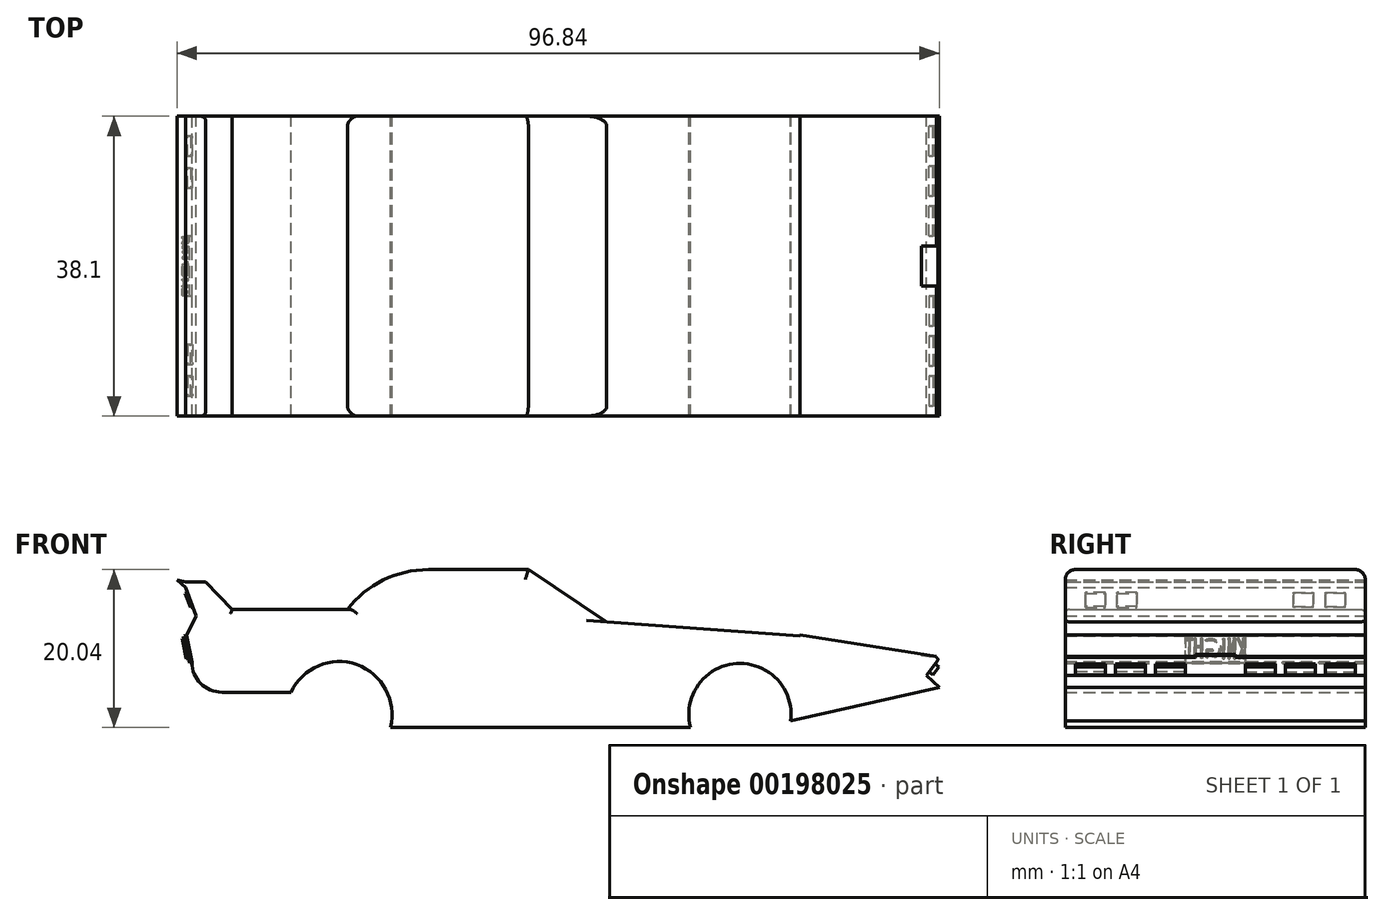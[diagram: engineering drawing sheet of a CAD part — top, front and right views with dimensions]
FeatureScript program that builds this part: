
annotation { "Feature Type Name" : "Feature", "Feature Type Description" : "" }
export const myFeature = defineFeature(function(context is Context, id is Id, definition is map)
    precondition{}
    {
        {
            var Q0;
            Q0=qCreatedBy(makeId("Front.planeOp"),FACE);
            var sketch = newSketch(context, id + "F0", { "sketchPlane" : qUnion([Q0])});
            skArc(sketch, "E0", {"start": v(4.17, 0.8) * mm, "mid": v(-2.68, 8.11) * mm, "end": v(-8.56, 0) * mm});
            skLineSegment(sketch, "E1", {"start": v(-8.56, 0) * mm, "end": v(-46.66, 0) * mm});
            skArc(sketch, "E2", {"start": v(-46.66, 0) * mm, "mid": v(-50.95, 7.97) * mm, "end": v(-59.3, 4.46) * mm});
            skLineSegment(sketch, "E3", {"start": v(-59.3, 4.46) * mm, "end": v(-68.07, 4.46) * mm});
            skLineSegment(sketch, "E4", {"start": v(-71.88, 8.27) * mm, "end": v(-72.57, 11.67) * mm});
            skLineSegment(sketch, "E5", {"start": v(-72.7, 18.5) * mm, "end": v(-70.16, 18.5) * mm});
            skLineSegment(sketch, "E6", {"start": v(-70.16, 18.5) * mm, "end": v(-66.76, 14.96) * mm});
            skLineSegment(sketch, "E7", {"start": v(-66.76, 14.96) * mm, "end": v(-52.11, 14.96) * mm});
            skLineSegment(sketch, "E8", {"start": v(-41.85, 20.04) * mm, "end": v(-29.15, 20.04) * mm});
            skArc(sketch, "E9", {"start": v(-41.85, 20.04) * mm, "mid": v(-47.58, 18.7) * mm, "end": v(-52.11, 14.96) * mm});
            skLineSegment(sketch, "E10", {"start": v(-29.15, 20.04) * mm, "end": v(-19.19, 13.37) * mm});
            skLineSegment(sketch, "E11", {"start": v(-19.19, 13.37) * mm, "end": v(5.34, 11.62) * mm});
            skLineSegment(sketch, "E12", {"start": v(5.34, 11.62) * mm, "end": v(23.06, 8.8) * mm});
            skLineSegment(sketch, "E13", {"start": v(23.06, 5.06) * mm, "end": v(4.17, 0.8) * mm});
            skLineSegment(sketch, "E14", {"start": v(23.06, 8.8) * mm, "end": v(21.44, 6.62) * mm});
            skLineSegment(sketch, "E15", {"start": v(21.44, 6.62) * mm, "end": v(23.06, 5.06) * mm});
            skPoint(sketch, "E16.visualSharp", {"position": v(-71.88, 4.46) * mm});
            skArc(sketch, "E16.filletArc", {"start": v(-71.88, 8.27) * mm, "mid": v(-70.77, 5.57) * mm, "end": v(-68.07, 4.46) * mm});
            skPoint(sketch, "E17.orphan", {"position": v(-59.72, 0) * mm});
            skPoint(sketch, "E18.orphan", {"position": v(4.02, 0) * mm});
            skLineSegment(sketch, "E19", {"start": v(-72.7, 18.5) * mm, "end": v(-73.78, 18.73) * mm});
            skLineSegment(sketch, "E20", {"start": v(-73.78, 18.73) * mm, "end": v(-72.7, 17.78) * mm});
            skLineSegment(sketch, "E21", {"start": v(-72.57, 11.67) * mm, "end": v(-71.32, 14.18) * mm});
            skLineSegment(sketch, "E22", {"start": v(-71.32, 14.18) * mm, "end": v(-72.7, 17.78) * mm});
            skSolve(sketch);
        }
        {
            var Q0;
            Q0=makeQuery(id+"F0.imprint","IMPRINT",FACE,{"disambiguationData":[TD([[makeQuery(id+"F0.imprint","IMPRINT",EDGE,{"derivedFrom":sQuery(id+"F0.wireOp",EDGE,"E0")}),-1.0]])]});
            extrude(context, id + "F1", {"entities" : qUnion([Q0]), "endBound" : BoundingType.SYMMETRIC, "depth" : 38.1 * mm});
        }
        {
            var Q0;
            {var subQ0=sQuery(id+"F0.wireOp",EDGE,"piWAozd6-odN5-IXnD-0DmP-VUwjhF2xC87r");var subQ1=sQuery(id+"F0.wireOp",EDGE,"E12");Q0=makeQuery(id+"FV3Uu7cO5sznl1Z_1.boolean.opBoolean","SPLIT",EDGE,{"disambiguationData":[TD([makeQuery(id+"FV3Uu7cO5sznl1Z_1.opExtrude","SWEPT_FACE",FACE,{"disambiguationData":[OSD([sQuery(id+"F6OuYayMSvIZY2Q_1.wireOp",EDGE,"LOxPacLx-S5zq-svhU-HEBB-QED5wKVLpIEs.right")])]})])],"derivedFrom":makeQuery(id+"F1.opExtrude","SWEPT_EDGE",EDGE,{"disambiguationData":[OSD([subQ1,subQ0])]})});}
            var Q1;
            Q1=makeQuery(id+"FV3Uu7cO5sznl1Z_1.boolean.opBoolean","INTERSECT",EDGE,{"derivedFrom":[makeQuery(id+"F1.opExtrude","SWEPT_FACE",FACE,{"disambiguationData":[OSD([sQuery(id+"F0.wireOp",EDGE,"piWAozd6-odN5-IXnD-0DmP-VUwjhF2xC87r")])]}),makeQuery(id+"FV3Uu7cO5sznl1Z_1.opExtrude","CAP_FACE",FACE,{"disambiguationData":[OSD([sQuery(id+"F6OuYayMSvIZY2Q_1.wireOp",EDGE,"LOxPacLx-S5zq-svhU-HEBB-QED5wKVLpIEs.bottom"),sQuery(id+"F6OuYayMSvIZY2Q_1.wireOp",EDGE,"LOxPacLx-S5zq-svhU-HEBB-QED5wKVLpIEs.top"),sQuery(id+"F6OuYayMSvIZY2Q_1.wireOp",EDGE,"LOxPacLx-S5zq-svhU-HEBB-QED5wKVLpIEs.left"),sQuery(id+"F6OuYayMSvIZY2Q_1.wireOp",EDGE,"LOxPacLx-S5zq-svhU-HEBB-QED5wKVLpIEs.right")])],"isStart":false})]});
            var Q2;
            {var subQ0=sQuery(id+"F0.wireOp",EDGE,"E12");var subQ1=sQuery(id+"F0.wireOp",EDGE,"piWAozd6-odN5-IXnD-0DmP-VUwjhF2xC87r");Q2=makeQuery(id+"FV3Uu7cO5sznl1Z_1.boolean.opBoolean","SPLIT",EDGE,{"disambiguationData":[TD([makeQuery(id+"FV3Uu7cO5sznl1Z_1.opExtrude","SWEPT_FACE",FACE,{"disambiguationData":[OSD([sQuery(id+"F6OuYayMSvIZY2Q_1.wireOp",EDGE,"r52KYWLg-ahqb-8f3H-ltxH-kNGmeAsnRNuQ.right")])]})])],"derivedFrom":makeQuery(id+"F1.opExtrude","SWEPT_EDGE",EDGE,{"disambiguationData":[OSD([subQ0,subQ1])]})});}
            var Q3;
            Q3=makeQuery(id+"FV3Uu7cO5sznl1Z_1.boolean.opBoolean","INTERSECT",EDGE,{"derivedFrom":[makeQuery(id+"F1.opExtrude","SWEPT_FACE",FACE,{"disambiguationData":[OSD([sQuery(id+"F0.wireOp",EDGE,"piWAozd6-odN5-IXnD-0DmP-VUwjhF2xC87r")])]}),makeQuery(id+"FV3Uu7cO5sznl1Z_1.opExtrude","CAP_FACE",FACE,{"disambiguationData":[OSD([sQuery(id+"F6OuYayMSvIZY2Q_1.wireOp",EDGE,"r52KYWLg-ahqb-8f3H-ltxH-kNGmeAsnRNuQ.bottom"),sQuery(id+"F6OuYayMSvIZY2Q_1.wireOp",EDGE,"r52KYWLg-ahqb-8f3H-ltxH-kNGmeAsnRNuQ.top"),sQuery(id+"F6OuYayMSvIZY2Q_1.wireOp",EDGE,"r52KYWLg-ahqb-8f3H-ltxH-kNGmeAsnRNuQ.left"),sQuery(id+"F6OuYayMSvIZY2Q_1.wireOp",EDGE,"r52KYWLg-ahqb-8f3H-ltxH-kNGmeAsnRNuQ.right")])],"isStart":false})]});
            var Q4;
            {var subQ0=sQuery(id+"F0.wireOp",EDGE,"E12");var subQ1=sQuery(id+"F0.wireOp",EDGE,"piWAozd6-odN5-IXnD-0DmP-VUwjhF2xC87r");Q4=makeQuery(id+"FV3Uu7cO5sznl1Z_1.boolean.opBoolean","SPLIT",EDGE,{"disambiguationData":[TD([makeQuery(id+"FV3Uu7cO5sznl1Z_1.opExtrude","SWEPT_FACE",FACE,{"disambiguationData":[OSD([sQuery(id+"F6OuYayMSvIZY2Q_1.wireOp",EDGE,"NTCnOCoN-yu8C-SXyQ-er5I-QvQ5yvy4iVEx.right")])]})])],"derivedFrom":makeQuery(id+"F1.opExtrude","SWEPT_EDGE",EDGE,{"disambiguationData":[OSD([subQ0,subQ1])]})});}
            var Q5;
            Q5=makeQuery(id+"FV3Uu7cO5sznl1Z_1.boolean.opBoolean","INTERSECT",EDGE,{"derivedFrom":[makeQuery(id+"F1.opExtrude","SWEPT_FACE",FACE,{"disambiguationData":[OSD([sQuery(id+"F0.wireOp",EDGE,"piWAozd6-odN5-IXnD-0DmP-VUwjhF2xC87r")])]}),makeQuery(id+"FV3Uu7cO5sznl1Z_1.opExtrude","CAP_FACE",FACE,{"disambiguationData":[OSD([sQuery(id+"F6OuYayMSvIZY2Q_1.wireOp",EDGE,"NTCnOCoN-yu8C-SXyQ-er5I-QvQ5yvy4iVEx.bottom"),sQuery(id+"F6OuYayMSvIZY2Q_1.wireOp",EDGE,"NTCnOCoN-yu8C-SXyQ-er5I-QvQ5yvy4iVEx.top"),sQuery(id+"F6OuYayMSvIZY2Q_1.wireOp",EDGE,"NTCnOCoN-yu8C-SXyQ-er5I-QvQ5yvy4iVEx.left"),sQuery(id+"F6OuYayMSvIZY2Q_1.wireOp",EDGE,"NTCnOCoN-yu8C-SXyQ-er5I-QvQ5yvy4iVEx.right")])],"isStart":false})]});
            var Q6;
            {var subQ0=sQuery(id+"F0.wireOp",EDGE,"E12");var subQ1=sQuery(id+"F0.wireOp",EDGE,"piWAozd6-odN5-IXnD-0DmP-VUwjhF2xC87r");Q6=makeQuery(id+"FV3Uu7cO5sznl1Z_1.boolean.opBoolean","SPLIT",EDGE,{"disambiguationData":[TD([makeQuery(id+"FV3Uu7cO5sznl1Z_1.opExtrude","SWEPT_FACE",FACE,{"disambiguationData":[OSD([sQuery(id+"F6OuYayMSvIZY2Q_1.wireOp",EDGE,"9fj7zr7S-9n9s-cSpx-WFiQ-eEYzpOB873Fi.right")])]})])],"derivedFrom":makeQuery(id+"F1.opExtrude","SWEPT_EDGE",EDGE,{"disambiguationData":[OSD([subQ0,subQ1])]})});}
            var Q7;
            Q7=makeQuery(id+"FV3Uu7cO5sznl1Z_1.boolean.opBoolean","INTERSECT",EDGE,{"derivedFrom":[makeQuery(id+"F1.opExtrude","SWEPT_FACE",FACE,{"disambiguationData":[OSD([sQuery(id+"F0.wireOp",EDGE,"piWAozd6-odN5-IXnD-0DmP-VUwjhF2xC87r")])]}),makeQuery(id+"FV3Uu7cO5sznl1Z_1.opExtrude","CAP_FACE",FACE,{"disambiguationData":[OSD([sQuery(id+"F6OuYayMSvIZY2Q_1.wireOp",EDGE,"9fj7zr7S-9n9s-cSpx-WFiQ-eEYzpOB873Fi.bottom"),sQuery(id+"F6OuYayMSvIZY2Q_1.wireOp",EDGE,"9fj7zr7S-9n9s-cSpx-WFiQ-eEYzpOB873Fi.top"),sQuery(id+"F6OuYayMSvIZY2Q_1.wireOp",EDGE,"9fj7zr7S-9n9s-cSpx-WFiQ-eEYzpOB873Fi.left"),sQuery(id+"F6OuYayMSvIZY2Q_1.wireOp",EDGE,"9fj7zr7S-9n9s-cSpx-WFiQ-eEYzpOB873Fi.right")])],"isStart":false})]});
            var Q8;
            {var subQ0=sQuery(id+"F0.wireOp",EDGE,"E12");var subQ1=sQuery(id+"F0.wireOp",EDGE,"piWAozd6-odN5-IXnD-0DmP-VUwjhF2xC87r");Q8=makeQuery(id+"FV3Uu7cO5sznl1Z_1.boolean.opBoolean","SPLIT",EDGE,{"disambiguationData":[TD([makeQuery(id+"FV3Uu7cO5sznl1Z_1.opExtrude","SWEPT_FACE",FACE,{"disambiguationData":[OSD([sQuery(id+"F6OuYayMSvIZY2Q_1.wireOp",EDGE,"LBPB0bUL-G7kI-9L5E-pr7f-Sai9KsrLVXPn.right")])]})])],"derivedFrom":makeQuery(id+"F1.opExtrude","SWEPT_EDGE",EDGE,{"disambiguationData":[OSD([subQ0,subQ1])]})});}
            var Q9;
            Q9=makeQuery(id+"FV3Uu7cO5sznl1Z_1.boolean.opBoolean","INTERSECT",EDGE,{"derivedFrom":[makeQuery(id+"F1.opExtrude","SWEPT_FACE",FACE,{"disambiguationData":[OSD([sQuery(id+"F0.wireOp",EDGE,"piWAozd6-odN5-IXnD-0DmP-VUwjhF2xC87r")])]}),makeQuery(id+"FV3Uu7cO5sznl1Z_1.opExtrude","CAP_FACE",FACE,{"disambiguationData":[OSD([sQuery(id+"F6OuYayMSvIZY2Q_1.wireOp",EDGE,"LBPB0bUL-G7kI-9L5E-pr7f-Sai9KsrLVXPn.bottom"),sQuery(id+"F6OuYayMSvIZY2Q_1.wireOp",EDGE,"LBPB0bUL-G7kI-9L5E-pr7f-Sai9KsrLVXPn.top"),sQuery(id+"F6OuYayMSvIZY2Q_1.wireOp",EDGE,"LBPB0bUL-G7kI-9L5E-pr7f-Sai9KsrLVXPn.left"),sQuery(id+"F6OuYayMSvIZY2Q_1.wireOp",EDGE,"LBPB0bUL-G7kI-9L5E-pr7f-Sai9KsrLVXPn.right")])],"isStart":false})]});
            var Q10;
            {var subQ0=sQuery(id+"F0.wireOp",EDGE,"E12");var subQ1=sQuery(id+"F0.wireOp",EDGE,"piWAozd6-odN5-IXnD-0DmP-VUwjhF2xC87r");Q10=makeQuery(id+"FV3Uu7cO5sznl1Z_1.boolean.opBoolean","SPLIT",EDGE,{"disambiguationData":[TD([makeQuery(id+"FV3Uu7cO5sznl1Z_1.opExtrude","SWEPT_FACE",FACE,{"disambiguationData":[OSD([sQuery(id+"F6OuYayMSvIZY2Q_1.wireOp",EDGE,"LBPB0bUL-G7kI-9L5E-pr7f-Sai9KsrLVXPn.left")])]})])],"derivedFrom":makeQuery(id+"F1.opExtrude","SWEPT_EDGE",EDGE,{"disambiguationData":[OSD([subQ0,subQ1])]})});}
            var Q11;
            Q11=makeQuery(id+"FV3Uu7cO5sznl1Z_1.boolean.opBoolean","INTERSECT",EDGE,{"derivedFrom":[makeQuery(id+"F1.opExtrude","SWEPT_FACE",FACE,{"disambiguationData":[OSD([sQuery(id+"F0.wireOp",EDGE,"piWAozd6-odN5-IXnD-0DmP-VUwjhF2xC87r")])]}),makeQuery(id+"FV3Uu7cO5sznl1Z_1.opExtrude","CAP_FACE",FACE,{"disambiguationData":[OSD([sQuery(id+"F6OuYayMSvIZY2Q_1.wireOp",EDGE,"508af859-bfde-4d98-a90f-149fa62f811b0.MirrorCS"),sQuery(id+"F6OuYayMSvIZY2Q_1.wireOp",EDGE,"37228f31-ebda-4232-9122-c2d6d20dc8920.MirrorCS"),sQuery(id+"F6OuYayMSvIZY2Q_1.wireOp",EDGE,"360aa123-8f3f-4f13-a378-a52a7b43db5a0.MirrorCS"),sQuery(id+"F6OuYayMSvIZY2Q_1.wireOp",EDGE,"0596e637-3ff4-463e-845c-65e150e65c670.MirrorCS")])],"isStart":false})]});
            var Q12;
            {var subQ0=sQuery(id+"F0.wireOp",EDGE,"E12");var subQ1=sQuery(id+"F0.wireOp",EDGE,"piWAozd6-odN5-IXnD-0DmP-VUwjhF2xC87r");Q12=makeQuery(id+"FV3Uu7cO5sznl1Z_1.boolean.opBoolean","SPLIT",EDGE,{"disambiguationData":[TD([makeQuery(id+"FV3Uu7cO5sznl1Z_1.opExtrude","SWEPT_FACE",FACE,{"disambiguationData":[OSD([sQuery(id+"F6OuYayMSvIZY2Q_1.wireOp",EDGE,"360aa123-8f3f-4f13-a378-a52a7b43db5a0.MirrorCS")])]})])],"derivedFrom":makeQuery(id+"F1.opExtrude","SWEPT_EDGE",EDGE,{"disambiguationData":[OSD([subQ0,subQ1])]})});}
            var Q13;
            Q13=makeQuery(id+"FV3Uu7cO5sznl1Z_1.boolean.opBoolean","INTERSECT",EDGE,{"derivedFrom":[makeQuery(id+"F1.opExtrude","SWEPT_FACE",FACE,{"disambiguationData":[OSD([sQuery(id+"F0.wireOp",EDGE,"piWAozd6-odN5-IXnD-0DmP-VUwjhF2xC87r")])]}),makeQuery(id+"FV3Uu7cO5sznl1Z_1.opExtrude","CAP_FACE",FACE,{"disambiguationData":[OSD([sQuery(id+"F6OuYayMSvIZY2Q_1.wireOp",EDGE,"bb352b80-0b1b-409d-a26b-4e7a8cd47cef0.MirrorCS"),sQuery(id+"F6OuYayMSvIZY2Q_1.wireOp",EDGE,"cf446a10-7582-4012-8e6f-7b8a887e3fab0.MirrorCS"),sQuery(id+"F6OuYayMSvIZY2Q_1.wireOp",EDGE,"d08ecadf-17e7-492c-b659-bda2cb3b14340.MirrorCS"),sQuery(id+"F6OuYayMSvIZY2Q_1.wireOp",EDGE,"e908241f-848e-4f62-8962-ae2c5000804a0.MirrorCS")])],"isStart":false})]});
            var Q14;
            {var subQ0=sQuery(id+"F0.wireOp",EDGE,"E12");var subQ1=sQuery(id+"F0.wireOp",EDGE,"piWAozd6-odN5-IXnD-0DmP-VUwjhF2xC87r");Q14=makeQuery(id+"FV3Uu7cO5sznl1Z_1.boolean.opBoolean","SPLIT",EDGE,{"disambiguationData":[TD([makeQuery(id+"FV3Uu7cO5sznl1Z_1.opExtrude","SWEPT_FACE",FACE,{"disambiguationData":[OSD([sQuery(id+"F6OuYayMSvIZY2Q_1.wireOp",EDGE,"cf446a10-7582-4012-8e6f-7b8a887e3fab0.MirrorCS")])]})])],"derivedFrom":makeQuery(id+"F1.opExtrude","SWEPT_EDGE",EDGE,{"disambiguationData":[OSD([subQ0,subQ1])]})});}
            var Q15;
            Q15=makeQuery(id+"FV3Uu7cO5sznl1Z_1.boolean.opBoolean","INTERSECT",EDGE,{"derivedFrom":[makeQuery(id+"F1.opExtrude","SWEPT_FACE",FACE,{"disambiguationData":[OSD([sQuery(id+"F0.wireOp",EDGE,"piWAozd6-odN5-IXnD-0DmP-VUwjhF2xC87r")])]}),makeQuery(id+"FV3Uu7cO5sznl1Z_1.opExtrude","CAP_FACE",FACE,{"disambiguationData":[OSD([sQuery(id+"F6OuYayMSvIZY2Q_1.wireOp",EDGE,"8a9b0b0e-97b4-4ba9-a973-1c92080a53030.MirrorCS"),sQuery(id+"F6OuYayMSvIZY2Q_1.wireOp",EDGE,"3b6446a7-c2c3-40b9-9697-2142afb4b24a0.MirrorCS"),sQuery(id+"F6OuYayMSvIZY2Q_1.wireOp",EDGE,"c94ae0a3-7226-48b3-982c-0a8c260cbade0.MirrorCS"),sQuery(id+"F6OuYayMSvIZY2Q_1.wireOp",EDGE,"839fec6f-e18f-459d-ad96-e984b2c5d6d60.MirrorCS")])],"isStart":false})]});
            var Q16;
            {var subQ0=sQuery(id+"F0.wireOp",EDGE,"E12");var subQ1=sQuery(id+"F0.wireOp",EDGE,"piWAozd6-odN5-IXnD-0DmP-VUwjhF2xC87r");Q16=makeQuery(id+"FV3Uu7cO5sznl1Z_1.boolean.opBoolean","SPLIT",EDGE,{"disambiguationData":[TD([makeQuery(id+"FV3Uu7cO5sznl1Z_1.opExtrude","SWEPT_FACE",FACE,{"disambiguationData":[OSD([sQuery(id+"F6OuYayMSvIZY2Q_1.wireOp",EDGE,"839fec6f-e18f-459d-ad96-e984b2c5d6d60.MirrorCS")])]})])],"derivedFrom":makeQuery(id+"F1.opExtrude","SWEPT_EDGE",EDGE,{"disambiguationData":[OSD([subQ0,subQ1])]})});}
            var Q17;
            Q17=makeQuery(id+"FV3Uu7cO5sznl1Z_1.boolean.opBoolean","INTERSECT",EDGE,{"derivedFrom":[makeQuery(id+"F1.opExtrude","SWEPT_FACE",FACE,{"disambiguationData":[OSD([sQuery(id+"F0.wireOp",EDGE,"piWAozd6-odN5-IXnD-0DmP-VUwjhF2xC87r")])]}),makeQuery(id+"FV3Uu7cO5sznl1Z_1.opExtrude","CAP_FACE",FACE,{"disambiguationData":[OSD([sQuery(id+"F6OuYayMSvIZY2Q_1.wireOp",EDGE,"05967368-317e-4f26-8281-6c34b3c6d1e60.MirrorCS"),sQuery(id+"F6OuYayMSvIZY2Q_1.wireOp",EDGE,"10d03c6d-404a-41d4-ac66-de4be596f0e30.MirrorCS"),sQuery(id+"F6OuYayMSvIZY2Q_1.wireOp",EDGE,"09338377-e241-4c4c-a4fa-bf4e565ec6370.MirrorCS"),sQuery(id+"F6OuYayMSvIZY2Q_1.wireOp",EDGE,"4262b961-d854-423d-87d7-c21d2e8108a90.MirrorCS")])],"isStart":false})]});
            var Q18;
            {var subQ0=sQuery(id+"F0.wireOp",EDGE,"E12");var subQ1=sQuery(id+"F0.wireOp",EDGE,"piWAozd6-odN5-IXnD-0DmP-VUwjhF2xC87r");Q18=makeQuery(id+"FV3Uu7cO5sznl1Z_1.boolean.opBoolean","SPLIT",EDGE,{"disambiguationData":[TD([makeQuery(id+"FV3Uu7cO5sznl1Z_1.opExtrude","SWEPT_FACE",FACE,{"disambiguationData":[OSD([sQuery(id+"F6OuYayMSvIZY2Q_1.wireOp",EDGE,"10d03c6d-404a-41d4-ac66-de4be596f0e30.MirrorCS")])]})])],"derivedFrom":makeQuery(id+"F1.opExtrude","SWEPT_EDGE",EDGE,{"disambiguationData":[OSD([subQ0,subQ1])]})});}
            var Q19;
            Q19=makeQuery(id+"FV3Uu7cO5sznl1Z_1.boolean.opBoolean","INTERSECT",EDGE,{"derivedFrom":[makeQuery(id+"F1.opExtrude","SWEPT_FACE",FACE,{"disambiguationData":[OSD([sQuery(id+"F0.wireOp",EDGE,"piWAozd6-odN5-IXnD-0DmP-VUwjhF2xC87r")])]}),makeQuery(id+"FV3Uu7cO5sznl1Z_1.opExtrude","CAP_FACE",FACE,{"disambiguationData":[OSD([sQuery(id+"F6OuYayMSvIZY2Q_1.wireOp",EDGE,"74e5a05d-e68e-48eb-8f2f-b1d45a82cd280.MirrorCS"),sQuery(id+"F6OuYayMSvIZY2Q_1.wireOp",EDGE,"93f09404-d1ae-43cb-bdeb-6ca15733254d0.MirrorCS"),sQuery(id+"F6OuYayMSvIZY2Q_1.wireOp",EDGE,"a1cbbde3-3219-4e6b-ba27-ff48f55d945b0.MirrorCS"),sQuery(id+"F6OuYayMSvIZY2Q_1.wireOp",EDGE,"cdac1700-6b11-4df6-9001-883cc821f1520.MirrorCS")])],"isStart":false})]});
            var Q20;
            {var subQ0=sQuery(id+"F0.wireOp",EDGE,"piWAozd6-odN5-IXnD-0DmP-VUwjhF2xC87r");var subQ1=sQuery(id+"F0.wireOp",EDGE,"E12");Q20=makeQuery(id+"FV3Uu7cO5sznl1Z_1.boolean.opBoolean","SPLIT",EDGE,{"disambiguationData":[TD([makeQuery(id+"FV3Uu7cO5sznl1Z_1.opExtrude","SWEPT_FACE",FACE,{"disambiguationData":[OSD([sQuery(id+"F6OuYayMSvIZY2Q_1.wireOp",EDGE,"a1cbbde3-3219-4e6b-ba27-ff48f55d945b0.MirrorCS")])]})])],"derivedFrom":makeQuery(id+"F1.opExtrude","SWEPT_EDGE",EDGE,{"disambiguationData":[OSD([subQ1,subQ0])]})});}
            fillet(context, id + "F2", {"entities" : qUnion([Q0, Q1, Q2, Q3, Q4, Q5, Q6, Q7, Q8, Q9, Q10, Q11, Q12, Q13, Q14, Q15, Q16, Q17, Q18, Q19, Q20]), "radius" : 0.25 * mm, "tangentPropagation" : true, "allowEdgeOverflow" : false});
        }
        {
            var Q0;
            Q0=makeQuery(id+"F1.opExtrude","SWEPT_FACE",FACE,{"disambiguationData":[OSD([sQuery(id+"F0.wireOp",EDGE,"E14")])]});
            var sketch = newSketch(context, id + "F3", { "sketchPlane" : qUnion([Q0])});
            skLineSegment(sketch, "E23", {"start": v(0, 20.4) * mm, "end": v(0, 18.12) * mm});
            skLineSegment(sketch, "E24", {"start": v(0, 20.4) * mm, "end": v(-3.81, 20.4) * mm});
            skLineSegment(sketch, "E25.bottom", {"start": v(-3.8, 19.9) * mm, "end": v(-7.62, 19.9) * mm});
            skLineSegment(sketch, "E25.top", {"start": v(-3.8, 18.63) * mm, "end": v(-7.62, 18.63) * mm});
            skLineSegment(sketch, "E25.left", {"start": v(-3.8, 19.9) * mm, "end": v(-3.8, 18.63) * mm});
            skLineSegment(sketch, "E25.right", {"start": v(-7.62, 19.9) * mm, "end": v(-7.62, 18.63) * mm});
            skLineSegment(sketch, "E26.bottom", {"start": v(-8.9, 19.9) * mm, "end": v(-12.7, 19.9) * mm});
            skLineSegment(sketch, "E26.top", {"start": v(-8.9, 18.63) * mm, "end": v(-12.7, 18.63) * mm});
            skLineSegment(sketch, "E26.left", {"start": v(-8.9, 19.9) * mm, "end": v(-8.9, 18.63) * mm});
            skLineSegment(sketch, "E26.right", {"start": v(-12.7, 19.9) * mm, "end": v(-12.7, 18.63) * mm});
            skLineSegment(sketch, "E27.bottom", {"start": v(-13.97, 19.9) * mm, "end": v(-17.78, 19.9) * mm});
            skLineSegment(sketch, "E27.top", {"start": v(-13.97, 18.63) * mm, "end": v(-17.78, 18.63) * mm});
            skLineSegment(sketch, "E27.left", {"start": v(-13.97, 19.9) * mm, "end": v(-13.97, 18.63) * mm});
            skLineSegment(sketch, "E27.right", {"start": v(-17.78, 19.9) * mm, "end": v(-17.78, 18.63) * mm});
            skLineSegment(sketch, "E28.MirrorCS", {"start": v(3.8, 19.9) * mm, "end": v(7.62, 19.9) * mm});
            skLineSegment(sketch, "E29.MirrorCS", {"start": v(3.8, 19.9) * mm, "end": v(3.8, 18.63) * mm});
            skLineSegment(sketch, "E30.MirrorCS", {"start": v(3.8, 18.63) * mm, "end": v(7.62, 18.63) * mm});
            skLineSegment(sketch, "E31.MirrorCS", {"start": v(7.62, 19.9) * mm, "end": v(7.62, 18.63) * mm});
            skLineSegment(sketch, "E32.MirrorCS", {"start": v(8.9, 19.9) * mm, "end": v(8.9, 18.63) * mm});
            skLineSegment(sketch, "E33.MirrorCS", {"start": v(8.9, 19.9) * mm, "end": v(12.7, 19.9) * mm});
            skLineSegment(sketch, "E34.MirrorCS", {"start": v(8.9, 18.63) * mm, "end": v(12.7, 18.63) * mm});
            skLineSegment(sketch, "E35.MirrorCS", {"start": v(12.7, 19.9) * mm, "end": v(12.7, 18.63) * mm});
            skLineSegment(sketch, "E36.MirrorCS", {"start": v(13.97, 19.9) * mm, "end": v(13.97, 18.63) * mm});
            skLineSegment(sketch, "E37.MirrorCS", {"start": v(13.97, 19.9) * mm, "end": v(17.78, 19.9) * mm});
            skLineSegment(sketch, "E38.MirrorCS", {"start": v(17.78, 19.9) * mm, "end": v(17.78, 18.63) * mm});
            skLineSegment(sketch, "E39.MirrorCS", {"start": v(13.97, 18.63) * mm, "end": v(17.78, 18.63) * mm});
            skSolve(sketch);
        }
        {
            var Q0;
            Q0=makeQuery(id+"F3.imprint","IMPRINT",FACE,{"disambiguationData":[TD([[makeQuery(id+"F3.imprint","IMPRINT",EDGE,{"derivedFrom":sQuery(id+"F3.wireOp",EDGE,"E27.bottom")}),1.0]])]});
            var Q1;
            Q1=makeQuery(id+"F3.imprint","IMPRINT",FACE,{"disambiguationData":[TD([[makeQuery(id+"F3.imprint","IMPRINT",EDGE,{"derivedFrom":sQuery(id+"F3.wireOp",EDGE,"E26.bottom")}),1.0]])]});
            var Q2;
            Q2=makeQuery(id+"F3.imprint","IMPRINT",FACE,{"disambiguationData":[TD([[makeQuery(id+"F3.imprint","IMPRINT",EDGE,{"derivedFrom":sQuery(id+"F3.wireOp",EDGE,"E25.bottom")}),1.0]])]});
            var Q3;
            Q3=makeQuery(id+"F3.imprint","IMPRINT",FACE,{"disambiguationData":[TD([[makeQuery(id+"F3.imprint","IMPRINT",EDGE,{"derivedFrom":sQuery(id+"F3.wireOp",EDGE,"E28.MirrorCS")}),-1.0]])]});
            var Q4;
            Q4=makeQuery(id+"F3.imprint","IMPRINT",FACE,{"disambiguationData":[TD([[makeQuery(id+"F3.imprint","IMPRINT",EDGE,{"derivedFrom":sQuery(id+"F3.wireOp",EDGE,"E32.MirrorCS")}),1.0]])]});
            var Q5;
            Q5=makeQuery(id+"F3.imprint","IMPRINT",FACE,{"disambiguationData":[TD([[makeQuery(id+"F3.imprint","IMPRINT",EDGE,{"derivedFrom":sQuery(id+"F3.wireOp",EDGE,"E36.MirrorCS")}),1.0]])]});
            extrude(context, id + "F4", {"entities" : qUnion([Q0, Q1, Q2, Q3, Q4, Q5]), "operationType" : NewBodyOperationType.ADD, "endBound" : BoundingType.SYMMETRIC, "oppositeDirection" : true, "depth" : 1.27 * mm});
        }
        {
            var Q0;
            Q0=makeQuery(id+"F1.opExtrude","SWEPT_FACE",FACE,{"disambiguationData":[OSD([sQuery(id+"F0.wireOp",EDGE,"E12")])]});
            var sketch = newSketch(context, id + "F5", { "sketchPlane" : qUnion([Q0])});
            skLineSegment(sketch, "E40.bottom", {"start": v(20.97, -2.54) * mm, "end": v(19.07, -2.54) * mm});
            skLineSegment(sketch, "E40.top", {"start": v(20.97, 2.54) * mm, "end": v(19.07, 2.54) * mm});
            skLineSegment(sketch, "E40.left", {"start": v(20.97, -2.54) * mm, "end": v(20.97, 2.54) * mm});
            skLineSegment(sketch, "E40.right", {"start": v(19.07, -2.54) * mm, "end": v(19.07, 2.54) * mm});
            skSolve(sketch);
        }
        {
            var Q0;
            {var subQ4=sQuery(id+"F5.wireOp",EDGE,"E40.bottom");Q0=makeQuery(id+"F5.imprint","IMPRINT",FACE,{"disambiguationData":[TD([[makeQuery(id+"F5.imprint","IMPRINT",EDGE,{"derivedFrom":subQ4}),1.0]])]});}
            extrude(context, id + "F6", {"entities" : qUnion([Q0]), "operationType" : NewBodyOperationType.ADD, "endBound" : BoundingType.SYMMETRIC, "depth" : 0.25 * mm});
        }
        {
            var Q0;
            Q0=makeQuery(id+"F1.opExtrude","CAP_EDGE",EDGE,{"disambiguationData":[OSD([sQuery(id+"F0.wireOp",EDGE,"E8")])],"isStart":true});
            var Q1;
            Q1=makeQuery(id+"F1.opExtrude","CAP_EDGE",EDGE,{"disambiguationData":[OSD([sQuery(id+"F0.wireOp",EDGE,"E8")])],"isStart":false});
            var Q2;
            Q2=makeQuery(id+"F1.opExtrude","CAP_EDGE",EDGE,{"disambiguationData":[OSD([sQuery(id+"F0.wireOp",EDGE,"E10")])],"isStart":false});
            var Q3;
            Q3=makeQuery(id+"F1.opExtrude","CAP_EDGE",EDGE,{"disambiguationData":[OSD([sQuery(id+"F0.wireOp",EDGE,"E10")])],"isStart":true});
            var Q4;
            Q4=makeQuery(id+"F1.opExtrude","CAP_EDGE",EDGE,{"disambiguationData":[OSD([sQuery(id+"F0.wireOp",EDGE,"E9")])],"isStart":false});
            var Q5;
            Q5=makeQuery(id+"F1.opExtrude","CAP_EDGE",EDGE,{"disambiguationData":[OSD([sQuery(id+"F0.wireOp",EDGE,"E9")])],"isStart":true});
            fillet(context, id + "F7", {"entities" : qUnion([Q0, Q1, Q2, Q3, Q4, Q5]), "radius" : 1.27 * mm, "tangentPropagation" : true, "allowEdgeOverflow" : false});
        }
        {
            var Q0;
            Q0=makeQuery(id+"F1.opExtrude","CAP_EDGE",EDGE,{"disambiguationData":[OSD([sQuery(id+"F0.wireOp",EDGE,"E7")])],"isStart":false});
            var Q1;
            Q1=makeQuery(id+"F1.opExtrude","CAP_EDGE",EDGE,{"disambiguationData":[OSD([sQuery(id+"F0.wireOp",EDGE,"E7")])],"isStart":true});
            var Q2;
            Q2=makeQuery(id+"F1.opExtrude","CAP_EDGE",EDGE,{"disambiguationData":[OSD([sQuery(id+"F0.wireOp",EDGE,"E6")])],"isStart":false});
            var Q3;
            Q3=makeQuery(id+"F1.opExtrude","CAP_EDGE",EDGE,{"disambiguationData":[OSD([sQuery(id+"F0.wireOp",EDGE,"E6")])],"isStart":true});
            fillet(context, id + "F8", {"entities" : qUnion([Q0, Q1, Q2, Q3]), "radius" : 0.5 * mm, "tangentPropagation" : true, "allowEdgeOverflow" : false});
        }
        {
            var Q0;
            Q0=makeQuery(id+"F1.opExtrude","SWEPT_FACE",FACE,{"disambiguationData":[OSD([sQuery(id+"F0.wireOp",EDGE,"E22")])]});
            var sketch = newSketch(context, id + "F9", { "sketchPlane" : qUnion([Q0])});
            skLineSegment(sketch, "E41.bottom", {"start": v(-16.51, 41.84) * mm, "end": v(-13.97, 41.84) * mm});
            skLineSegment(sketch, "E41.top", {"start": v(-16.51, 39.94) * mm, "end": v(-13.97, 39.94) * mm});
            skLineSegment(sketch, "E41.left", {"start": v(-16.5, 41.84) * mm, "end": v(-16.5, 39.94) * mm});
            skLineSegment(sketch, "E41.right", {"start": v(-13.97, 41.84) * mm, "end": v(-13.97, 39.94) * mm});
            skLineSegment(sketch, "E42.bottom", {"start": v(-12.47, 39.94) * mm, "end": v(-9.93, 39.94) * mm});
            skLineSegment(sketch, "E42.top", {"start": v(-12.47, 41.84) * mm, "end": v(-9.93, 41.84) * mm});
            skLineSegment(sketch, "E42.left", {"start": v(-12.47, 39.94) * mm, "end": v(-12.47, 41.84) * mm});
            skLineSegment(sketch, "E42.right", {"start": v(-9.93, 39.94) * mm, "end": v(-9.93, 41.84) * mm});
            skLineSegment(sketch, "E43.MirrorCS", {"start": v(9.93, 39.94) * mm, "end": v(9.93, 41.84) * mm});
            skLineSegment(sketch, "E44.MirrorCS", {"start": v(12.47, 41.84) * mm, "end": v(9.93, 41.84) * mm});
            skLineSegment(sketch, "E45.MirrorCS", {"start": v(12.47, 39.94) * mm, "end": v(9.93, 39.94) * mm});
            skLineSegment(sketch, "E46.MirrorCS", {"start": v(12.47, 39.94) * mm, "end": v(12.47, 41.84) * mm});
            skLineSegment(sketch, "E47.MirrorCS", {"start": v(16.51, 41.84) * mm, "end": v(13.97, 41.84) * mm});
            skLineSegment(sketch, "E48.MirrorCS", {"start": v(16.5, 41.84) * mm, "end": v(16.5, 39.94) * mm});
            skLineSegment(sketch, "E49.MirrorCS", {"start": v(16.51, 39.94) * mm, "end": v(13.97, 39.94) * mm});
            skLineSegment(sketch, "E50.MirrorCS", {"start": v(13.97, 41.84) * mm, "end": v(13.97, 39.94) * mm});
            skSolve(sketch);
        }
        {
            var Q0;
            Q0=makeQuery(id+"F9.imprint","IMPRINT",FACE,{"disambiguationData":[TD([[makeQuery(id+"F9.imprint","IMPRINT",EDGE,{"derivedFrom":sQuery(id+"F9.wireOp",EDGE,"E41.bottom")}),-1.0]])]});
            var Q1;
            Q1=makeQuery(id+"F9.imprint","IMPRINT",FACE,{"disambiguationData":[TD([[makeQuery(id+"F9.imprint","IMPRINT",EDGE,{"derivedFrom":sQuery(id+"F9.wireOp",EDGE,"E42.bottom")}),1.0]])]});
            var Q2;
            Q2=makeQuery(id+"F9.imprint","IMPRINT",FACE,{"disambiguationData":[TD([[makeQuery(id+"F9.imprint","IMPRINT",EDGE,{"derivedFrom":sQuery(id+"F9.wireOp",EDGE,"E43.MirrorCS")}),-1.0]])]});
            var Q3;
            Q3=makeQuery(id+"F9.imprint","IMPRINT",FACE,{"disambiguationData":[TD([[makeQuery(id+"F9.imprint","IMPRINT",EDGE,{"derivedFrom":sQuery(id+"F9.wireOp",EDGE,"E47.MirrorCS")}),1.0]])]});
            extrude(context, id + "F10", {"entities" : qUnion([Q0, Q1, Q2, Q3]), "operationType" : NewBodyOperationType.ADD, "endBound" : BoundingType.SYMMETRIC, "depth" : 0.64 * mm});
        }
        {
            var Q0;
            Q0=makeQuery(id+"F1.opExtrude","SWEPT_FACE",FACE,{"disambiguationData":[OSD([sQuery(id+"F0.wireOp",EDGE,"E4")])]});
            var sketch = newSketch(context, id + "F11", { "sketchPlane" : qUnion([Q0])});
            skLineSegment(sketch, "E51", {"start": v(0, 25.76) * mm, "end": v(-3.8, 25.76) * mm});
            skLineSegment(sketch, "E52.bottom", {"start": v(-3.8, 25.76) * mm, "end": v(3.81, 25.76) * mm});
            skLineSegment(sketch, "E52.top", {"start": v(-3.8, 22.3) * mm, "end": v(3.81, 22.3) * mm});
            skLineSegment(sketch, "E52.left", {"start": v(-3.8, 25.76) * mm, "end": v(-3.8, 22.3) * mm});
            skLineSegment(sketch, "E52.right", {"start": v(3.81, 25.76) * mm, "end": v(3.81, 22.3) * mm});
            skSolve(sketch);
        }
        {
            var Q0;
            Q0=makeQuery(id+"F11.imprint","IMPRINT",FACE,{"disambiguationData":[TD([[makeQuery(id+"F11.imprint","IMPRINT",EDGE,{"derivedFrom":sQuery(id+"F11.wireOp",EDGE,"E52.top")}),-1.0]])]});
            extrude(context, id + "F12", {"entities" : qUnion([Q0]), "operationType" : NewBodyOperationType.ADD, "endBound" : BoundingType.SYMMETRIC, "depth" : 0.64 * mm});
        }
        {
            var Q0;
            Q0=makeQuery(id+"F12.opExtrude","CAP_FACE",FACE,{"disambiguationData":[OSD([sQuery(id+"F11.wireOp",EDGE,"E52.bottom"),sQuery(id+"F11.wireOp",EDGE,"E52.top"),sQuery(id+"F11.wireOp",EDGE,"E52.left"),sQuery(id+"F11.wireOp",EDGE,"E52.right")])],"isStart":false});
            var sketch = newSketch(context, id + "F13", { "sketchPlane" : qUnion([Q0])});
            skLineSegment(sketch, "E53", {"start": v(-3.75, 25.5) * mm, "end": v(-3.75, 22.88) * mm});
            skLineSegment(sketch, "E54", {"start": v(-3.75, 22.88) * mm, "end": v(-3.5, 22.88) * mm});
            skLineSegment(sketch, "E55", {"start": v(-3.5, 22.88) * mm, "end": v(-3.5, 24.03) * mm});
            skLineSegment(sketch, "E56", {"start": v(-3.5, 24.03) * mm, "end": v(-3.16, 22.88) * mm});
            skLineSegment(sketch, "E57", {"start": v(-3.16, 22.88) * mm, "end": v(-2.94, 22.88) * mm});
            skLineSegment(sketch, "E58", {"start": v(-3.35, 24.15) * mm, "end": v(-2.83, 25.43) * mm});
            skLineSegment(sketch, "E59", {"start": v(-2.83, 25.43) * mm, "end": v(-3, 25.5) * mm});
            skLineSegment(sketch, "E60", {"start": v(-3, 25.5) * mm, "end": v(-3.5, 24.28) * mm});
            skLineSegment(sketch, "E61", {"start": v(-3.5, 24.28) * mm, "end": v(-3.5, 25.5) * mm});
            skLineSegment(sketch, "E62", {"start": v(-3.5, 25.5) * mm, "end": v(-3.75, 25.5) * mm});
            skLineSegment(sketch, "E63", {"start": v(-2.94, 22.88) * mm, "end": v(-3.35, 24.15) * mm});
            skLineSegment(sketch, "E64", {"start": v(-2.53, 22.88) * mm, "end": v(-2.53, 25.51) * mm});
            skLineSegment(sketch, "E65", {"start": v(-2.53, 25.51) * mm, "end": v(-2.33, 25.51) * mm});
            skLineSegment(sketch, "E66", {"start": v(-2.33, 25.51) * mm, "end": v(-1.84, 23.34) * mm});
            skLineSegment(sketch, "E67", {"start": v(-1.84, 25.51) * mm, "end": v(-1.7, 25.51) * mm});
            skLineSegment(sketch, "E68", {"start": v(-1.7, 25.51) * mm, "end": v(-1.7, 22.88) * mm});
            skLineSegment(sketch, "E69", {"start": v(-1.7, 22.88) * mm, "end": v(-1.84, 22.88) * mm});
            skLineSegment(sketch, "E70", {"start": v(-1.84, 22.88) * mm, "end": v(-2.38, 25.19) * mm});
            skLineSegment(sketch, "E71", {"start": v(-2.38, 25.19) * mm, "end": v(-2.38, 22.88) * mm});
            skLineSegment(sketch, "E72", {"start": v(-2.38, 22.88) * mm, "end": v(-2.53, 22.88) * mm});
            skLineSegment(sketch, "E73.trimOffspring", {"start": v(-1.84, 23.34) * mm, "end": v(-1.84, 25.51) * mm});
            skLineSegment(sketch, "E74", {"start": v(-1.16, 25.47) * mm, "end": v(-0.96, 25.47) * mm});
            skLineSegment(sketch, "E75", {"start": v(-0.96, 25.47) * mm, "end": v(-0.96, 22.88) * mm});
            skLineSegment(sketch, "E76", {"start": v(-0.96, 22.88) * mm, "end": v(-1.15, 22.88) * mm});
            skLineSegment(sketch, "E77", {"start": v(-1.15, 22.88) * mm, "end": v(-1.16, 25.47) * mm});
            skArc(sketch, "E78", {"start": v(1.25, 25.28) * mm, "mid": v(-0.67, 24.25) * mm, "end": v(1.12, 23.01) * mm});
            skLineSegment(sketch, "E79", {"start": v(1.12, 23.01) * mm, "end": v(1.12, 24.02) * mm});
            skLineSegment(sketch, "E80", {"start": v(1.12, 24.02) * mm, "end": v(0.27, 24.02) * mm});
            skLineSegment(sketch, "E81", {"start": v(0.27, 24.02) * mm, "end": v(0.27, 23.83) * mm});
            skLineSegment(sketch, "E82", {"start": v(0.27, 23.83) * mm, "end": v(0.92, 23.83) * mm});
            skLineSegment(sketch, "E83", {"start": v(0.92, 23.83) * mm, "end": v(0.92, 23.13) * mm});
            skLineSegment(sketch, "E84", {"start": v(1.25, 25.28) * mm, "end": v(1.15, 25.12) * mm});
            skArc(sketch, "E85", {"start": v(1.15, 25.12) * mm, "mid": v(-0.49, 24.3) * mm, "end": v(0.92, 23.13) * mm});
            skLineSegment(sketch, "E86", {"start": v(1.62, 25.5) * mm, "end": v(1.62, 22.9) * mm});
            skLineSegment(sketch, "E87", {"start": v(1.62, 22.9) * mm, "end": v(1.82, 22.9) * mm});
            skLineSegment(sketch, "E88", {"start": v(1.82, 22.9) * mm, "end": v(1.82, 24.28) * mm});
            skLineSegment(sketch, "E89", {"start": v(1.82, 24.28) * mm, "end": v(2.47, 24.28) * mm});
            skLineSegment(sketch, "E90", {"start": v(2.47, 24.28) * mm, "end": v(2.47, 22.9) * mm});
            skLineSegment(sketch, "E91", {"start": v(2.47, 22.9) * mm, "end": v(2.65, 22.9) * mm});
            skLineSegment(sketch, "E92", {"start": v(2.65, 22.9) * mm, "end": v(2.65, 25.5) * mm});
            skLineSegment(sketch, "E93", {"start": v(2.65, 25.5) * mm, "end": v(2.47, 25.49) * mm});
            skLineSegment(sketch, "E94", {"start": v(2.47, 25.49) * mm, "end": v(2.47, 24.49) * mm});
            skLineSegment(sketch, "E95", {"start": v(2.47, 24.49) * mm, "end": v(1.82, 24.49) * mm});
            skLineSegment(sketch, "E96", {"start": v(1.82, 24.49) * mm, "end": v(1.82, 25.5) * mm});
            skLineSegment(sketch, "E97", {"start": v(1.82, 25.5) * mm, "end": v(1.62, 25.5) * mm});
            skLineSegment(sketch, "E98", {"start": v(3.74, 25.27) * mm, "end": v(3.36, 25.27) * mm});
            skLineSegment(sketch, "E99", {"start": v(3.74, 25.27) * mm, "end": v(3.74, 25.49) * mm});
            skLineSegment(sketch, "E100", {"start": v(3.74, 25.49) * mm, "end": v(2.82, 25.49) * mm});
            skLineSegment(sketch, "E101", {"start": v(2.82, 25.49) * mm, "end": v(2.82, 25.27) * mm});
            skLineSegment(sketch, "E102", {"start": v(2.82, 25.27) * mm, "end": v(3.2, 25.27) * mm});
            skLineSegment(sketch, "E103", {"start": v(3.2, 25.27) * mm, "end": v(3.2, 22.9) * mm});
            skLineSegment(sketch, "E104", {"start": v(3.2, 22.9) * mm, "end": v(3.38, 22.9) * mm});
            skLineSegment(sketch, "E105", {"start": v(3.38, 22.9) * mm, "end": v(3.36, 25.27) * mm});
            skSolve(sketch);
        }
        {
            var Q0;
            Q0=makeQuery(id+"F13.imprint","IMPRINT",FACE,{"disambiguationData":[TD([[makeQuery(id+"F13.imprint","IMPRINT",EDGE,{"derivedFrom":sQuery(id+"F13.wireOp",EDGE,"E53")}),1.0]])]});
            var Q1;
            Q1=makeQuery(id+"F13.imprint","IMPRINT",FACE,{"disambiguationData":[TD([[makeQuery(id+"F13.imprint","IMPRINT",EDGE,{"derivedFrom":sQuery(id+"F13.wireOp",EDGE,"E64")}),-1.0]])]});
            var Q2;
            Q2=makeQuery(id+"F13.imprint","IMPRINT",FACE,{"disambiguationData":[TD([[makeQuery(id+"F13.imprint","IMPRINT",EDGE,{"derivedFrom":sQuery(id+"F13.wireOp",EDGE,"E74")}),-1.0]])]});
            var Q3;
            Q3=makeQuery(id+"F13.imprint","IMPRINT",FACE,{"disambiguationData":[TD([[makeQuery(id+"F13.imprint","IMPRINT",EDGE,{"derivedFrom":sQuery(id+"F13.wireOp",EDGE,"E78")}),1.0]])]});
            var Q4;
            Q4=makeQuery(id+"F13.imprint","IMPRINT",FACE,{"disambiguationData":[TD([[makeQuery(id+"F13.imprint","IMPRINT",EDGE,{"derivedFrom":sQuery(id+"F13.wireOp",EDGE,"E86")}),1.0]])]});
            var Q5;
            Q5=makeQuery(id+"F13.imprint","IMPRINT",FACE,{"disambiguationData":[TD([[makeQuery(id+"F13.imprint","IMPRINT",EDGE,{"derivedFrom":sQuery(id+"F13.wireOp",EDGE,"E98")}),-1.0]])]});
            extrude(context, id + "F14", {"entities" : qUnion([Q0, Q1, Q2, Q3, Q4, Q5]), "operationType" : NewBodyOperationType.ADD, "endBound" : BoundingType.SYMMETRIC, "depth" : 0.64 * mm});
        }
    });
